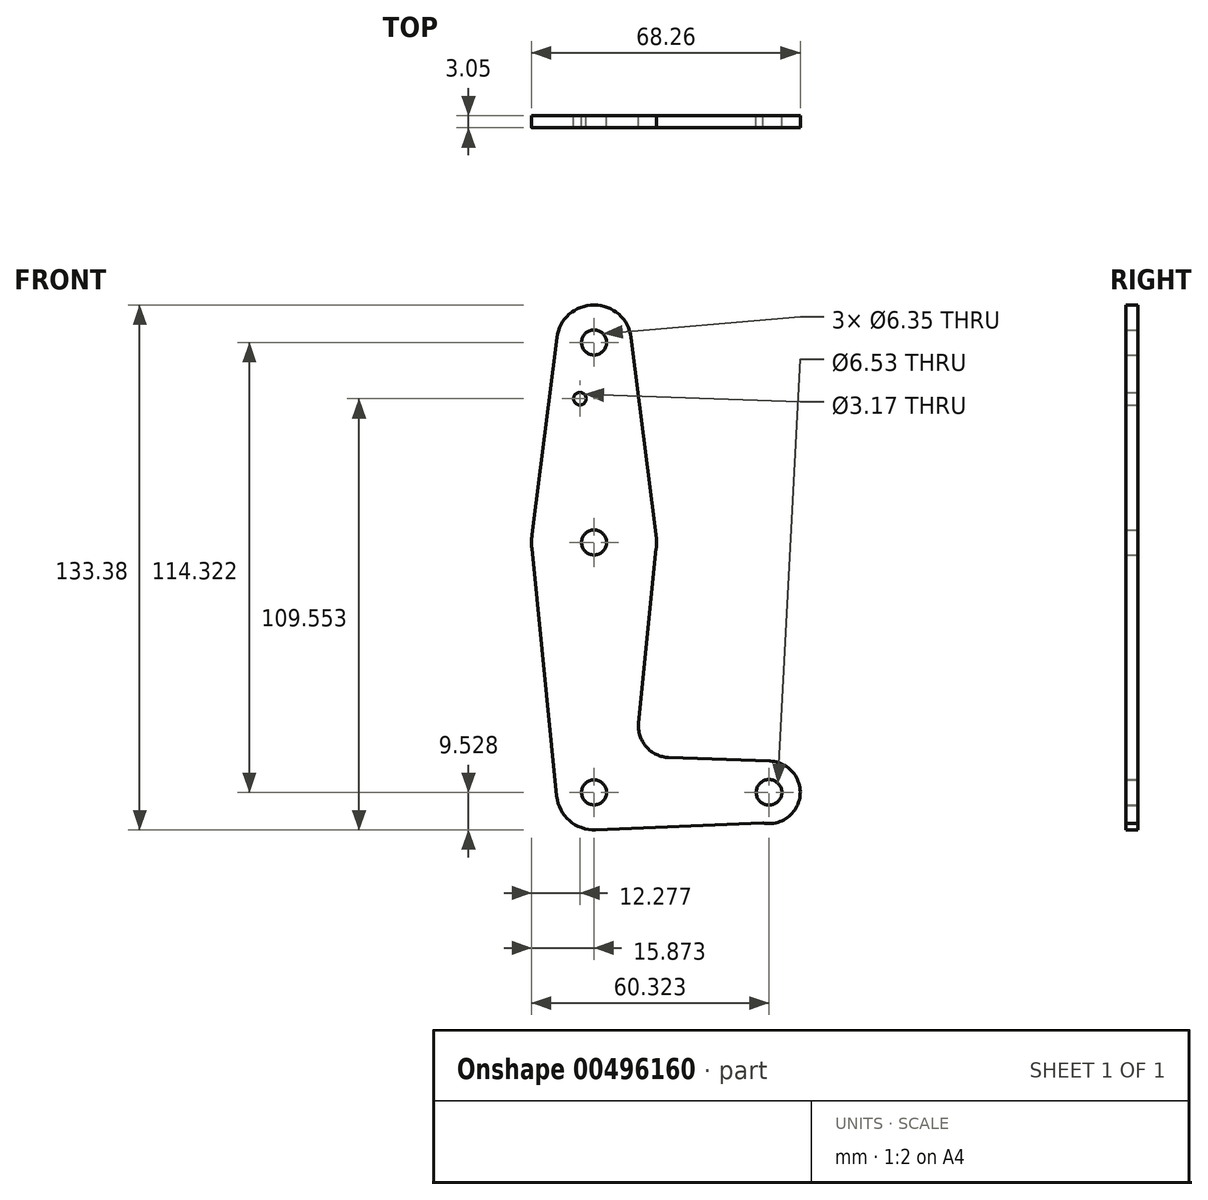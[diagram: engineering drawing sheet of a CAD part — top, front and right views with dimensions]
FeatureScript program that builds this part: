
annotation { "Feature Type Name" : "Feature", "Feature Type Description" : "" }
export const myFeature = defineFeature(function(context is Context, id is Id, definition is map)
    precondition{}
    {
        {
            var Q0;
            Q0=qCreatedBy(makeId("Front.planeOp"),FACE);
            var sketch = newSketch(context, id + "F0", { "sketchPlane" : qUnion([Q0])});
            skLineSegment(sketch, "E0", {"start": v(-0.39, -0.02) * mm, "end": v(-0.39, 114.3) * mm, "construction": true});
            skLineSegment(sketch, "E1", {"start": v(-0.39, -0.02) * mm, "end": v(44.06, -0.02) * mm, "construction": true});
            skCircle(sketch, "E2", {"center": v(-0.39, -0.02) * mm, "radius": 9.53 * mm});
            skCircle(sketch, "E3", {"center": v(-0.39, 63.48) * mm, "radius": 15.88 * mm});
            skCircle(sketch, "E4", {"center": v(44.06, -0.02) * mm, "radius": 7.94 * mm});
            skCircle(sketch, "E5", {"center": v(-0.39, 114.3) * mm, "radius": 9.53 * mm});
            skCircle(sketch, "E6", {"center": v(-0.39, 114.3) * mm, "radius": 3.18 * mm});
            skCircle(sketch, "E7", {"center": v(-3.98, 100) * mm, "radius": 1.59 * mm});
            skCircle(sketch, "E8", {"center": v(-0.39, 63.48) * mm, "radius": 3.18 * mm});
            skCircle(sketch, "E9", {"center": v(-0.39, -0.02) * mm, "radius": 3.18 * mm});
            skCircle(sketch, "E10", {"center": v(44.06, -0.02) * mm, "radius": 3.26 * mm});
            skLineSegment(sketch, "E11", {"start": v(-9.84, 115.5) * mm, "end": v(-16.14, 65.46) * mm});
            skLineSegment(sketch, "E12", {"start": v(-9.86, -0.97) * mm, "end": v(-16.18, 61.9) * mm});
            skLineSegment(sketch, "E13", {"start": v(9.06, 115.5) * mm, "end": v(15.36, 65.46) * mm});
            skLineSegment(sketch, "E14", {"start": v(15.4, 61.9) * mm, "end": v(10.95, 17.57) * mm});
            skLineSegment(sketch, "E15", {"start": v(18.58, 8.83) * mm, "end": v(44.35, 7.91) * mm});
            skLineSegment(sketch, "E16", {"start": v(0, -9.54) * mm, "end": v(46.23, -7.66) * mm});
            skArc(sketch, "E17.filletArc", {"start": v(10.95, 17.57) * mm, "mid": v(12.87, 11.55) * mm, "end": v(18.58, 8.83) * mm});
            skSolve(sketch);
        }
        {
            var Q0;
            Q0 = qSketchRegion(id + "F0", true);
            extrude(context, id + "F1", {"entities" : qUnion([Q0]), "depth" : 3.05 * mm, "offsetDistance" : 25.4 * mm});
        }
    });
